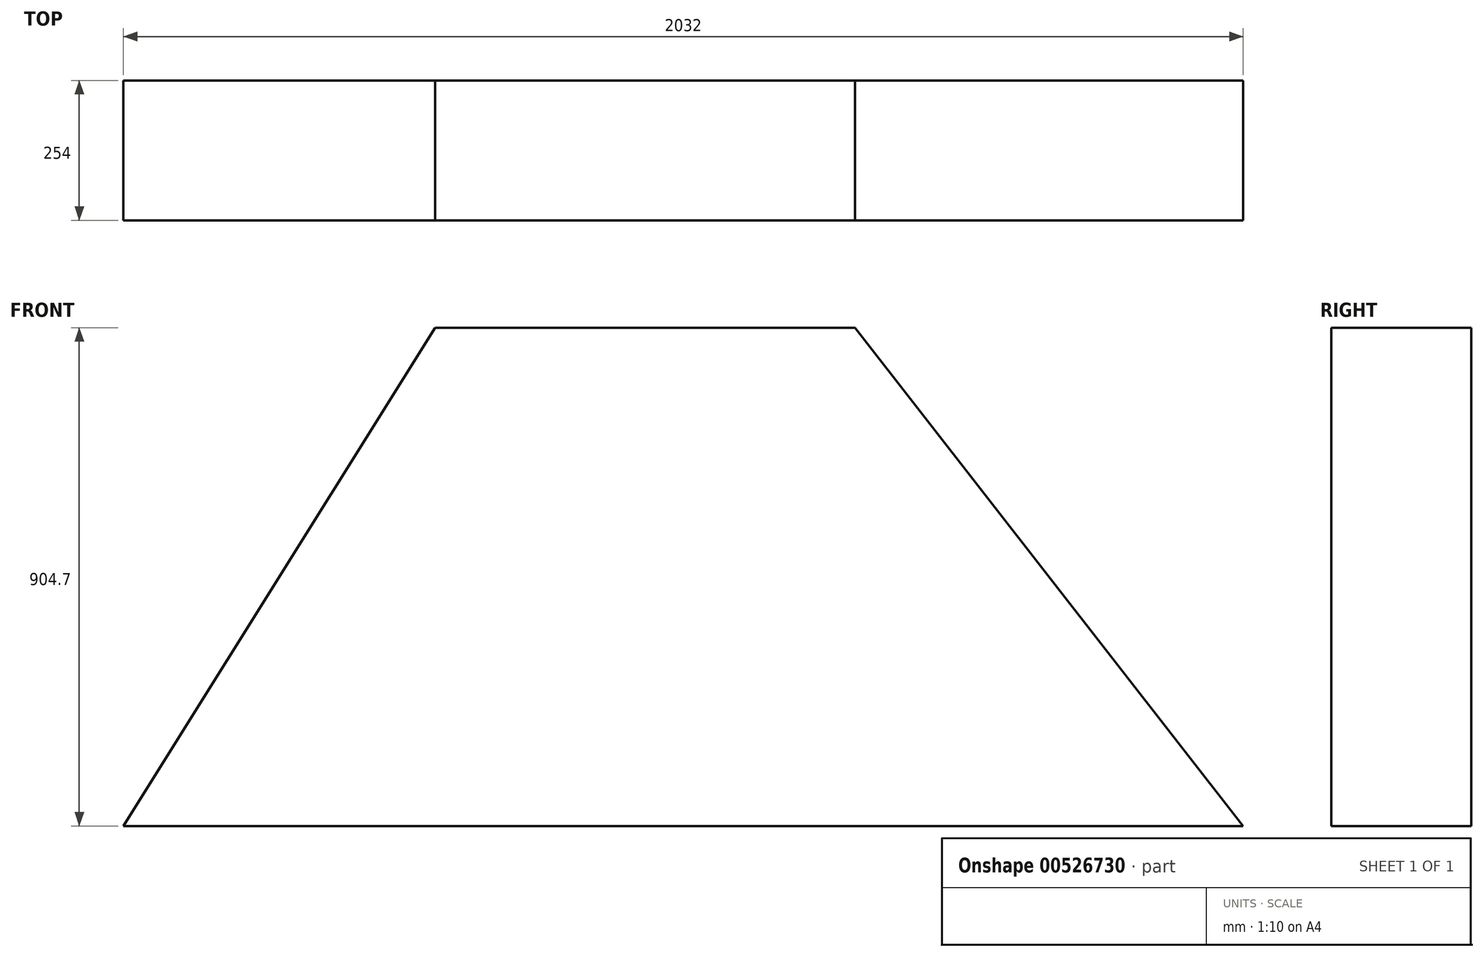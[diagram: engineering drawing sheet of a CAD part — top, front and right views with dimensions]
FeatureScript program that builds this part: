
annotation { "Feature Type Name" : "Feature", "Feature Type Description" : "" }
export const myFeature = defineFeature(function(context is Context, id is Id, definition is map)
    precondition{}
    {
        {
            var Q0;
            Q0=qCreatedBy(makeId("Front.planeOp"),FACE);
            var sketch = newSketch(context, id + "F0", { "sketchPlane" : qUnion([Q0])});
            skLineSegment(sketch, "E0", {"start": v(2.04, 0) * mm, "end": v(2034.04, 0) * mm});
            skLineSegment(sketch, "E1", {"start": v(2034.04, 0) * mm, "end": v(1329.36, 904.7) * mm});
            skLineSegment(sketch, "E2", {"start": v(1329.36, 904.7) * mm, "end": v(567.36, 904.7) * mm});
            skLineSegment(sketch, "E3", {"start": v(567.36, 904.7) * mm, "end": v(2.04, 0) * mm});
            skSolve(sketch);
        }
        {
            var Q0;
            Q0=makeQuery(id+"F0.imprint","IMPRINT",FACE,{"disambiguationData":[TD([[makeQuery(id+"F0.imprint","IMPRINT",EDGE,{"derivedFrom":sQuery(id+"F0.wireOp",EDGE,"E0")}),1.0]])]});
            extrude(context, id + "F1", {"entities" : qUnion([Q0]), "depth" : 254 * mm, "offsetDistance" : 25.4 * mm});
        }
    });
